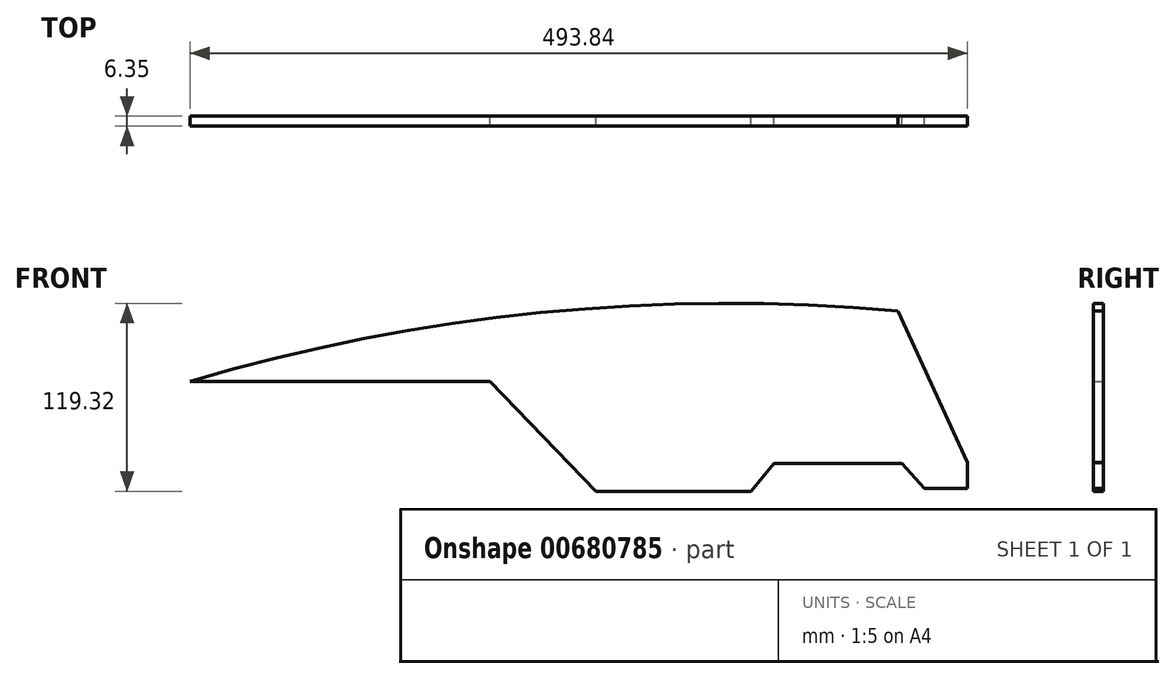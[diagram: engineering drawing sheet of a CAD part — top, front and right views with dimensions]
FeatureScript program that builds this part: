
annotation { "Feature Type Name" : "Feature", "Feature Type Description" : "" }
export const myFeature = defineFeature(function(context is Context, id is Id, definition is map)
    precondition{}
    {
        {
            var Q0;
            Q0=qCreatedBy(makeId("Front.planeOp"),FACE);
            var sketch = newSketch(context, id + "F0", { "sketchPlane" : qUnion([Q0])});
            skPoint(sketch, "E0.middle", {"position": v(0, 0) * mm});
            skLineSegment(sketch, "E1", {"start": v(-120.94, 12.85) * mm, "end": v(-311.62, 12.85) * mm});
            skLineSegment(sketch, "E2", {"start": v(-120.94, 12.85) * mm, "end": v(-53.66, -56.94) * mm});
            skLineSegment(sketch, "E3", {"start": v(-53.66, -56.94) * mm, "end": v(44.77, -56.94) * mm});
            skLineSegment(sketch, "E4", {"start": v(44.77, -56.94) * mm, "end": v(59.15, -39.27) * mm});
            skLineSegment(sketch, "E5", {"start": v(59.15, -39.27) * mm, "end": v(140.56, -39.27) * mm});
            skLineSegment(sketch, "E6", {"start": v(182.22, -55.03) * mm, "end": v(154.82, -55.03) * mm});
            skLineSegment(sketch, "E7", {"start": v(140.56, -39.27) * mm, "end": v(154.82, -55.03) * mm});
            skLineSegment(sketch, "E8", {"start": v(182.22, -38.58) * mm, "end": v(182.22, -55.03) * mm});
            skLineSegment(sketch, "E9", {"start": v(182.22, -38.58) * mm, "end": v(137.97, 57.56) * mm});
            skArc(sketch, "E10", {"start": v(137.97, 57.56) * mm, "mid": v(-88.94, 56.47) * mm, "end": v(-311.62, 12.85) * mm});
            skSolve(sketch);
        }
        {
            var Q0;
            Q0=makeQuery(id+"F0.imprint","IMPRINT",FACE,{"disambiguationData":[TD([[makeQuery(id+"F0.imprint","IMPRINT",EDGE,{"derivedFrom":sQuery(id+"F0.wireOp",EDGE,"E1")}),-1.0]])]});
            extrude(context, id + "F1", {"entities" : qUnion([Q0]), "depth" : 6.35 * mm, "offsetDistance" : 25.4 * mm});
        }
    });
